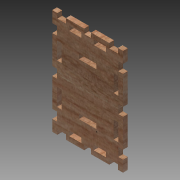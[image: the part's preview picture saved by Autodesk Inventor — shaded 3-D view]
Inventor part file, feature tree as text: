
AUTODESK INVENTOR PART (.ipt)
format: ipt  version: 2014 SP1 (Build 180222100, 222)  size: 407,552 bytes
history: native  units: mm
features: other x7, extrude x6, sketch x6
ambient origin geometry x8: Origin, YZ Plane, XZ Plane, XY Plane, X Axis, Y Axis, Z Axis, Center Point
bodies: Solid1 (feature_tree)
feature tree (19):
  other  "Blocks"
  extrude  "Extrusion1"  Depth=111.0mm
  extrude  "Extrusion2"  Depth=40.0mm
  extrude  "Extrusion13"  Depth=5.5mm
  extrude  "Extrusion15"  Depth=22.166667mm
  extrude  "Extrusion17"  Depth=14.2mm
  extrude  "Extrusion18"  Depth=10.0mm TaperAngle=0.0deg
  sketch  "Sketch1"  dims[d0=71.0mm d1=111.0mm]
  sketch  "Sketch6"  dims[d2=5.5mm d3=0.0mm d22=40.0mm]
  other  "Block1"
  other  "Block2"
  other  "Block3"
  other  "Block4"
  other  "Block5"
  other  "Block6"
  sketch  "Sketch26"  dims[d23=80.0mm d38=5.5mm]
  sketch  "Sketch27"  dims[d39=5.5mm d40=22.166667mm]
  sketch  "Sketch28"  dims[d41=20.0mm d42=14.2mm]
  sketch  "Sketch29"  dims[d43=14.2mm d44=10.0mm d45=0.0mm d59=11.0mm d60=5.0mm d62=11.0mm d63=5.0mm d126=5.5mm d127=5.5mm d128=5.5mm d129=0.0mm d132=5.0mm d133=10.0mm d137=5.5mm d138=0.0mm d139=4.0mm d140=5.5mm d141=10.0mm d142=5.5mm d146=5.5mm d147=0.0mm d148=25.0mm d149=38.0mm d150=20.0mm d151=5.5mm d152=60.0mm d153=5.5mm d154=0.0mm d26=1.0mm d27=1.0mm]
